# Revit family: Fan_Coil-With_Valve-Whalen-Vertical_Stacked-Classic-4P-No_Risers
name_source: partatom
category: Mechanical Equipment
revit_build: Autodesk Revit MEP 2012 (Build: 20110916_2132(x64)
units: mm (PartAtom-declared; Revit-internal decimal feet)

## types (6) — shared parameters
Date Last Modified = 2/12/2014
Description = See Part Description
Equipment Abbreviation = RFC
Family Version = 1.0.0
Load Classification = Other
Manufacturer = The Whalen Company
Model = See Part Number
Model Disclaimer = Contact The Whalen Company for More Information
Product Documentation Link = http://www.whalencompany.com
Product Material = Steel - Whalen - Galvanized
Provide Feedback = https://www.surveymonkey.com
URL = http://www.whalencompany.com

## per-type parameters (varying)
| type | zz Integer 7 |
| 0,300 CFM | 300 |
| 0,400 CFM | 400 |
| 0,600 CFM | 600 |
| 0,800 CFM | 800 |
| 1,000 CFM | 1000 |
| 1,200 CFM | 1200 |

## geometry (parser evidence)
native form markers: Blend x10, Sweep x7
no freeform markers — native parametric forms only
